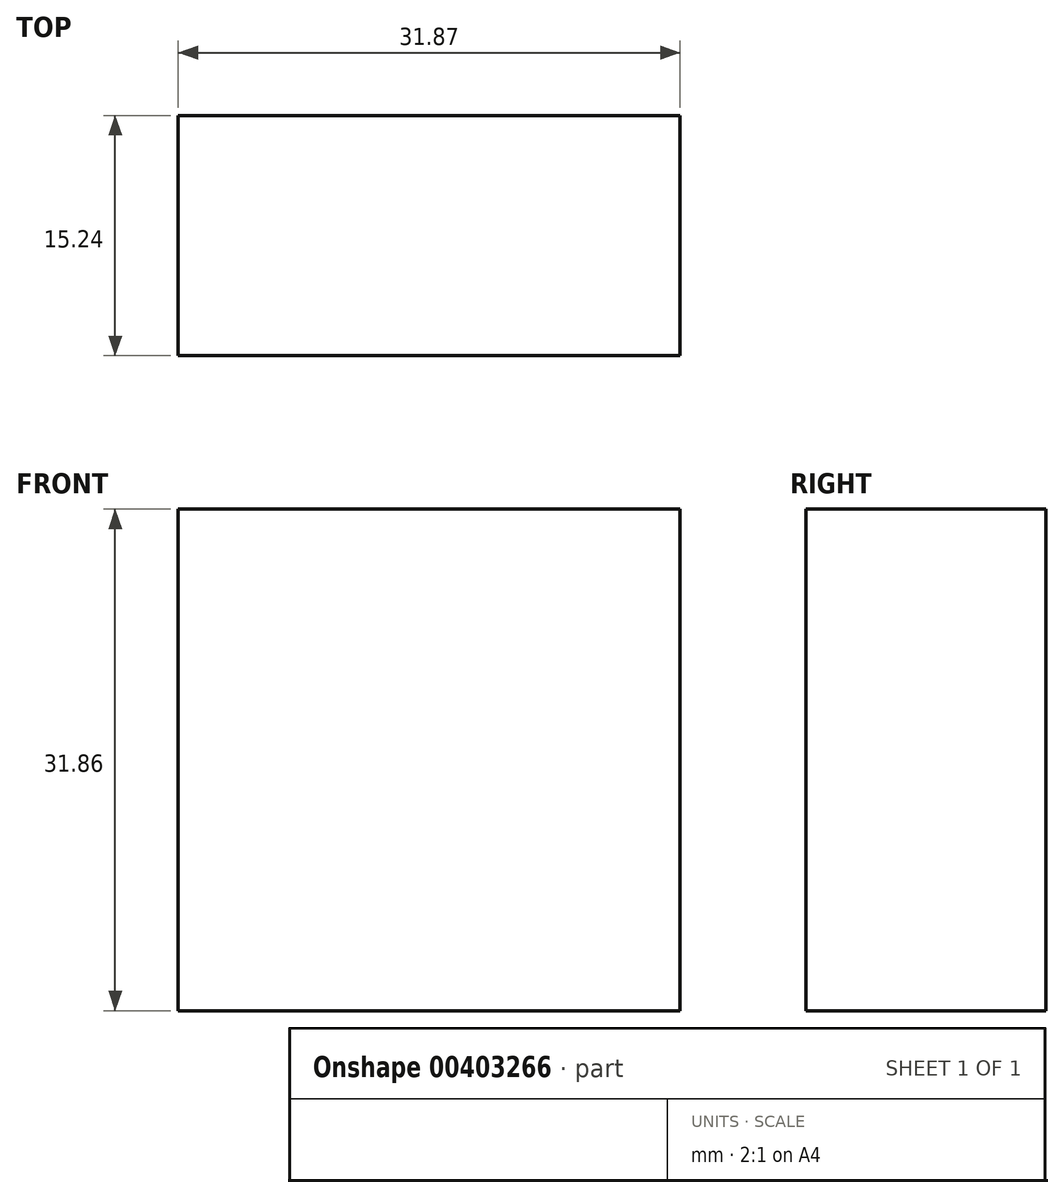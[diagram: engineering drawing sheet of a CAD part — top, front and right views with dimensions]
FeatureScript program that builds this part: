
annotation { "Feature Type Name" : "Feature", "Feature Type Description" : "" }
export const myFeature = defineFeature(function(context is Context, id is Id, definition is map)
    precondition{}
    {
        {
            var Q0;
            Q0=qCreatedBy(makeId("Front.planeOp"),FACE);
            var sketch = newSketch(context, id + "F0", { "sketchPlane" : qUnion([Q0])});
            skLineSegment(sketch, "E0.bottom", {"start": v(-31.87, 37.15) * mm, "end": v(0, 37.15) * mm});
            skLineSegment(sketch, "E0.top", {"start": v(-31.87, 5.29) * mm, "end": v(0, 5.29) * mm});
            skLineSegment(sketch, "E0.left", {"start": v(-31.87, 37.15) * mm, "end": v(-31.87, 5.29) * mm});
            skLineSegment(sketch, "E0.right", {"start": v(0, 37.15) * mm, "end": v(0, 5.29) * mm});
            skSolve(sketch);
        }
        {
            var Q0;
            Q0=qCreatedBy(makeId("Top.planeOp"),FACE);
            var sketch = newSketch(context, id + "F1", { "sketchPlane" : qUnion([Q0])});
            skFitSpline(sketch, "E1", {"points": [v(56.07, 11.06) * mm, v(31.42, 28.97) * mm, v(71.85, 34.44) * mm, v(37.42, 59.1) * mm, v(94.43, 51.94) * mm, v(121.5, 0) * mm], "startDerivative": vector(-274.22, 137.5) * mm, "endDerivative": vector(39.05, -266.65) * mm});
            skSolve(sketch);
        }
        {
            var Q0;
            Q0=makeQuery(id+"F0.imprint","IMPRINT",FACE,{"disambiguationData":[TD([[makeQuery(id+"F0.imprint","IMPRINT",EDGE,{"derivedFrom":sQuery(id+"F0.wireOp",EDGE,"E0.bottom")}),-1.0]])]});
            extrude(context, id + "F2", {"entities" : qUnion([Q0]), "depth" : 15.24 * mm});
        }
        {
            var Q0;
            Q0=makeQuery(id+"F1.imprint","IMPRINT",FACE,{"disambiguationData":[TD([[makeQuery(id+"F1.imprint","IMPRINT",EDGE,{"derivedFrom":sQuery(id+"F1.wireOp",EDGE,"dfe095d8-48be-41b7-83bf-36f6fb150ec2")}),-1.0]])]});
            var Q1;
            Q1=sQuery(id+"F1.wireOp",EDGE,"E1");
            extrude(context, id + "F3", {"entities" : qUnion([Q0]), "bodyType" : ToolBodyType.SURFACE, "surfaceEntities" : qUnion([Q1]), "oppositeDirection" : true, "depth" : 3.56 * mm});
        }
    });
